# Revit family: Storage-Vessel_AO_Smith-ST-3000_F
name_source: partatom
category: Mechanical Equipment
revit_build: Autodesk Revit 2016 (Build: 20170117_1200(x64)
units: mm (PartAtom-declared; Revit-internal decimal feet)

## family parameters
Always vertical = Yes
Cut with Voids When Loaded = No
OmniClass Number = 23.75.00.00
OmniClass Title = Climate Control (HVAC)
Part Type = Normal
Room Calculation Point = No
Round Connector Dimension = Use Radius
Shared = No
Work Plane-Based = No

## types (1)
- Storage-Vessel_AO_Smith-ST-3000_F
    1er Entretien (check-up) = 3 mois après l'installation
    2ème Entretien (Entretien Général) = 12 mois après l'installation
    Assembly Code = D3010
    BIM Content Developer = CAD & Company
    BIM Content Developer URL = http://www.cadcompany.nl
    Capacité - Cuve = 2820 m³
    Charge Maximale au Sol = 3340.00 kg
    Description = Ballon de Stockage
    Destination / Pays = France
    Diamètre (avec Isolation) = 1600 mm  [stored 5.24934 ft]
    Diamètre (sans Isolation) = 1400 mm  [stored 4.59318 ft]
    Epaisseur d'Isolation = 100 mm  [stored 0.328084 ft]
    Fabricant No. = E 7110
    Garantie Pièces = 12 mois
    Garantie sur la Cuve = 36 mois
    Guide de Produit = https://www.aosmithinternational.com
    Hauteur (avec Isolation) = 2070 mm  [stored 6.79134 ft]
    Hauteur (sans Isolation) = 2170 mm  [stored 7.11942 ft]
    Hauteur d'Emballage = 2195 mm
    Hauteur de l'Alimentation en eau Froide = 185 mm
    Hauteur de la Sortie d'eau Chaude = 2170 mm  [stored 7.11942 ft]
    Largeur d'Emballage = 1498 mm
    Manufacturer = A.O. Smith Water Products Company b.v.
    Max. Température de l'eau - Réservoir = 95 °C
    Model = ST 3000 F
    Nombre de modèle du produit (EAN) = 8717449172466
    Poids de Transport = 610.00 kg
    Poids à vide = 520.00 kg
    Pression de Service Maximale - Réservoir = 1000000.0 Pa
    Profondeur d'Emballage = 1680 mm
    Raccord d'Alimentation en Eau Froide = 2"
    Raccord de Sortie d'Eau Chaude = 2"
    Raccord de la Soupape de Vidange = 2"
    Spécifications du Produit = https://www.aosmithinternational.com
    Type d'Emballage = Plastique et Bois
    URL = http://www.aosmith.fr
    Workspace Diameter = 2600 mm  [stored 8.53018 ft]
    Workspace Height = 3070 mm  [stored 10.0722 ft]
    espace de travail = 1250 mm  [stored 4.10105 ft]
    l'Intervalle d'Entretien = 12 mois

note: [stored X ft] marks values corroborated as IEEE doubles in the binary element streams (Revit-internal decimal feet)

## geometry (parser evidence)
native form markers: Blend x4, Sweep x16
no freeform markers — native parametric forms only
